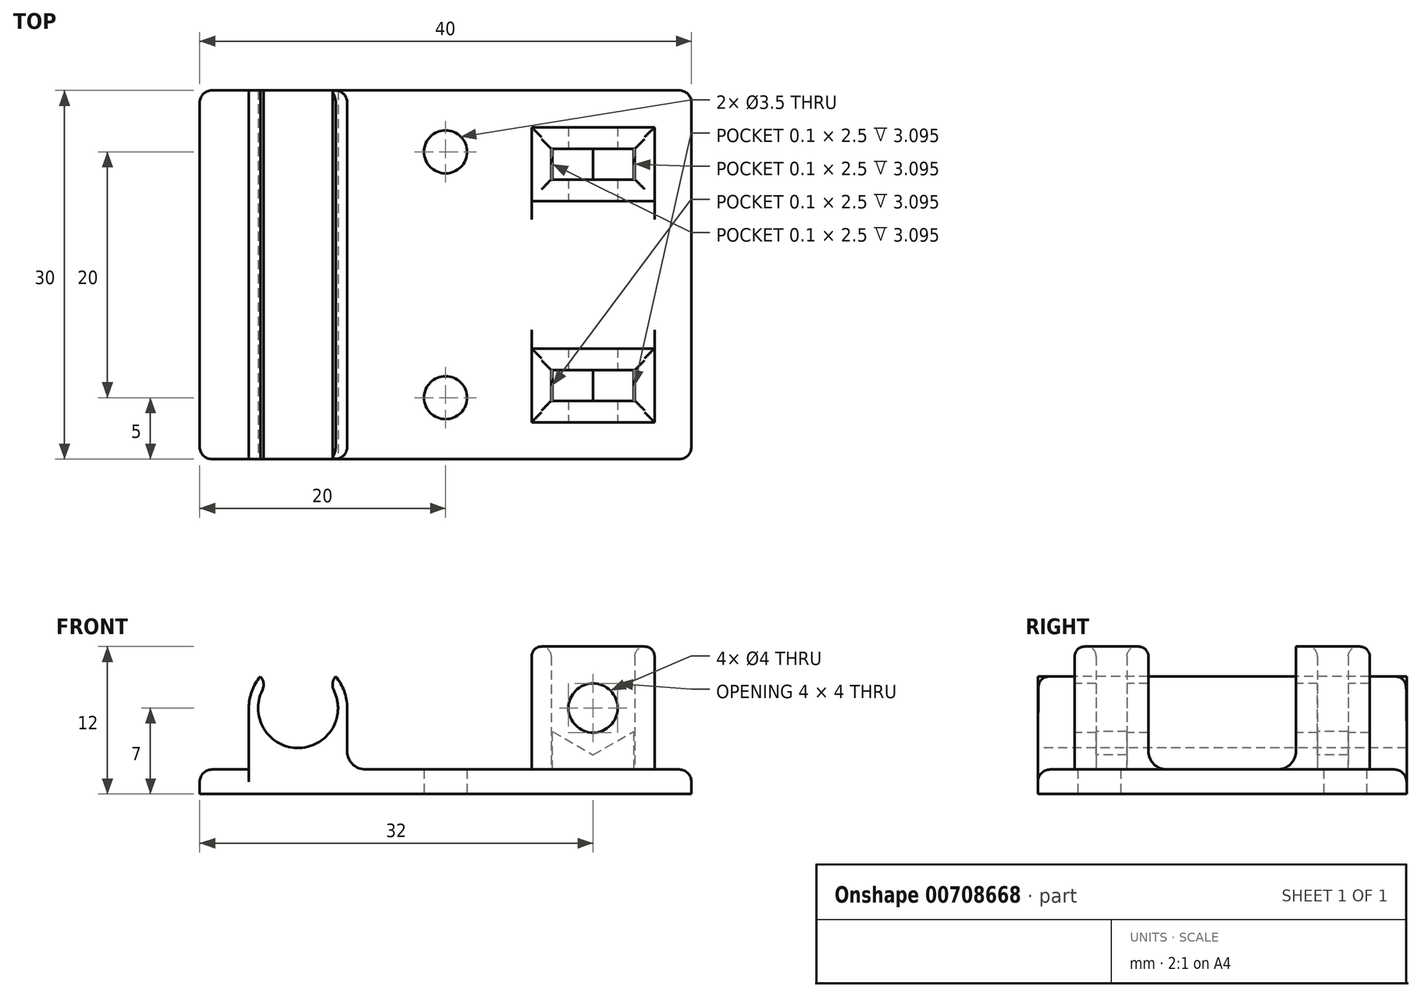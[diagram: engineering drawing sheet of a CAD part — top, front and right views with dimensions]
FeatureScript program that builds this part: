
annotation { "Feature Type Name" : "Feature", "Feature Type Description" : "" }
export const myFeature = defineFeature(function(context is Context, id is Id, definition is map)
    precondition{}
    {
        {
            var Q0;
            Q0=qCreatedBy(makeId("Top.planeOp"),FACE);
            var sketch = newSketch(context, id + "F0", { "sketchPlane" : qUnion([Q0])});
            skLineSegment(sketch, "E0.bottom", {"start": v(-20, 15) * mm, "end": v(20, 15) * mm});
            skLineSegment(sketch, "E0.top", {"start": v(-20, -15) * mm, "end": v(20, -15) * mm});
            skLineSegment(sketch, "E0.left", {"start": v(-20, 15) * mm, "end": v(-20, -15) * mm});
            skLineSegment(sketch, "E0.right", {"start": v(20, 15) * mm, "end": v(20, -15) * mm});
            skPoint(sketch, "E0.middle", {"position": v(0, 0) * mm});
            skLineSegment(sketch, "E1", {"start": v(12, 15) * mm, "end": v(12, 12) * mm, "construction": true});
            skLineSegment(sketch, "E2", {"start": v(7, -12) * mm, "end": v(17, -12) * mm});
            skLineSegment(sketch, "E3", {"start": v(17, -6) * mm, "end": v(7, -6) * mm});
            skLineSegment(sketch, "E4", {"start": v(7, 12) * mm, "end": v(17, 12) * mm});
            skLineSegment(sketch, "E5", {"start": v(17, -12) * mm, "end": v(17, -6) * mm});
            skLineSegment(sketch, "E6", {"start": v(17, 6) * mm, "end": v(7, 6) * mm});
            skLineSegment(sketch, "E7", {"start": v(7, 6) * mm, "end": v(7, 12) * mm});
            skLineSegment(sketch, "E8", {"start": v(17, 12) * mm, "end": v(17, 6) * mm});
            skLineSegment(sketch, "E9", {"start": v(7, -12) * mm, "end": v(7, -6) * mm});
            skLineSegment(sketch, "E10", {"start": v(12, 12) * mm, "end": v(12, 6) * mm, "construction": true});
            skLineSegment(sketch, "E11", {"start": v(12, 6) * mm, "end": v(12, -6) * mm, "construction": true});
            skLineSegment(sketch, "E12", {"start": v(12, -6) * mm, "end": v(12, -12) * mm, "construction": true});
            skLineSegment(sketch, "E13", {"start": v(12, -12) * mm, "end": v(12, -15) * mm, "construction": true});
            skLineSegment(sketch, "E14.bottom", {"start": v(8.6, -7.75) * mm, "end": v(15.4, -7.75) * mm});
            skLineSegment(sketch, "E14.top", {"start": v(8.6, -10.25) * mm, "end": v(15.4, -10.25) * mm});
            skLineSegment(sketch, "E14.left", {"start": v(8.6, -7.75) * mm, "end": v(8.6, -10.25) * mm});
            skLineSegment(sketch, "E14.right", {"start": v(15.4, -7.75) * mm, "end": v(15.4, -10.25) * mm});
            skPoint(sketch, "E14.middle", {"position": v(12, -9) * mm});
            skLineSegment(sketch, "E15.bottom", {"start": v(8.6, 7.75) * mm, "end": v(15.4, 7.75) * mm});
            skLineSegment(sketch, "E15.top", {"start": v(8.6, 10.25) * mm, "end": v(15.4, 10.25) * mm});
            skLineSegment(sketch, "E15.left", {"start": v(8.6, 7.75) * mm, "end": v(8.6, 10.25) * mm});
            skLineSegment(sketch, "E15.right", {"start": v(15.4, 7.75) * mm, "end": v(15.4, 10.25) * mm});
            skPoint(sketch, "E15.middle", {"position": v(12, 9) * mm});
            skLineSegment(sketch, "E16", {"start": v(7, -6) * mm, "end": v(7, 6) * mm});
            skLineSegment(sketch, "E17", {"start": v(17, 6) * mm, "end": v(17, -6) * mm});
            skLineSegment(sketch, "E18", {"start": v(-12, -15) * mm, "end": v(-12, 15) * mm, "construction": true});
            skCircle(sketch, "E19", {"center": v(0, 10) * mm, "radius": 1.75 * mm});
            skCircle(sketch, "E20", {"center": v(0, -10) * mm, "radius": 1.75 * mm});
            skSolve(sketch);
        }
        {
            var Q0;
            Q0=makeQuery(id+"F0.imprint","IMPRINT",FACE,{"disambiguationData":[TD([[makeQuery(id+"F0.imprint","IMPRINT",EDGE,{"derivedFrom":sQuery(id+"F0.wireOp",EDGE,"E0.bottom")}),-1.0]])]});
            var Q1;
            Q1=makeQuery(id+"F0.imprint","IMPRINT",FACE,{"disambiguationData":[TD([[makeQuery(id+"F0.imprint","IMPRINT",EDGE,{"derivedFrom":sQuery(id+"F0.wireOp",EDGE,"E15.bottom")}),1.0]])]});
            var Q2;
            Q2=makeQuery(id+"F0.imprint","IMPRINT",FACE,{"disambiguationData":[TD([[makeQuery(id+"F0.imprint","IMPRINT",EDGE,{"derivedFrom":sQuery(id+"F0.wireOp",EDGE,"E14.bottom")}),-1.0]])]});
            extrude(context, id + "F1", {"entities" : qUnion([Q0, Q1, Q2]), "depth" : 2 * mm, "offsetDistance" : 25 * mm});
        }
        {
            var Q0;
            Q0=makeQuery(id+"F0.imprint","IMPRINT",FACE,{"disambiguationData":[TD([[makeQuery(id+"F0.imprint","IMPRINT",EDGE,{"derivedFrom":sQuery(id+"F0.wireOp",EDGE,"E2")}),1.0]])]});
            var Q1;
            Q1=makeQuery(id+"F0.imprint","IMPRINT",FACE,{"disambiguationData":[TD([[makeQuery(id+"F0.imprint","IMPRINT",EDGE,{"derivedFrom":sQuery(id+"F0.wireOp",EDGE,"E4")}),-1.0]])]});
            var Q2;
            Q2=makeQuery(id+"F0.imprint","IMPRINT",FACE,{"disambiguationData":[TD([[makeQuery(id+"F0.imprint","IMPRINT",EDGE,{"derivedFrom":sQuery(id+"F0.wireOp",EDGE,"E3")}),-1.0]])]});
            extrude(context, id + "F2", {"entities" : qUnion([Q0, Q1, Q2]), "operationType" : NewBodyOperationType.ADD, "depth" : (2 + 10) * mm, "offsetDistance" : 25 * mm});
        }
        {
            var Q0;
            Q0=makeQuery(id+"F2.opExtrude","SWEPT_FACE",FACE,{"disambiguationData":[OSD([sQuery(id+"F0.wireOp",EDGE,"E2")])]});
            var sketch = newSketch(context, id + "F3", { "sketchPlane" : qUnion([Q0])});
            skLineSegment(sketch, "E21", {"start": v(7, 12) * mm, "end": v(17, 2) * mm, "construction": true});
            skCircle(sketch, "E22", {"center": v(12, 7) * mm, "radius": 2 * mm});
            skCircle(sketch, "E23.cCircle", {"center": v(12, 7) * mm, "radius": 3.3 * mm, "construction": true});
            skLineSegment(sketch, "E23.0", {"start": v(15.3, 8.9) * mm, "end": v(15.3, 5.1) * mm});
            skLineSegment(sketch, "E23.1", {"start": v(15.3, 5.1) * mm, "end": v(12, 3.19) * mm});
            skLineSegment(sketch, "E23.2", {"start": v(12, 3.19) * mm, "end": v(8.7, 5.1) * mm});
            skLineSegment(sketch, "E23.3", {"start": v(8.7, 5.1) * mm, "end": v(8.7, 8.9) * mm});
            skLineSegment(sketch, "E23.4", {"start": v(8.7, 8.9) * mm, "end": v(12, 10.81) * mm});
            skLineSegment(sketch, "E23.5", {"start": v(12, 10.81) * mm, "end": v(15.3, 8.9) * mm});
            skPoint(sketch, "E23.0.midPoint", {"position": v(15.3, 7) * mm});
            skLineSegment(sketch, "E24", {"start": v(8.7, 5.1) * mm, "end": v(8.7, 2) * mm});
            skLineSegment(sketch, "E25", {"start": v(8.7, 2) * mm, "end": v(15.3, 2) * mm});
            skLineSegment(sketch, "E26", {"start": v(15.3, 2) * mm, "end": v(15.3, 5.1) * mm});
            skSolve(sketch);
        }
        {
            var Q0;
            Q0=makeQuery(id+"F3.imprint","IMPRINT",FACE,{"disambiguationData":[TD([[makeQuery(id+"F3.imprint","IMPRINT",EDGE,{"derivedFrom":sQuery(id+"F3.wireOp",EDGE,"E22")}),1.0]])]});
            var Q1;
            Q1=makeQuery(id+"F2.opExtrude","SWEPT_FACE",FACE,{"disambiguationData":[OSD([sQuery(id+"F0.wireOp",EDGE,"E4")])]});
            extrude(context, id + "F4", {"entities" : qUnion([Q0]), "operationType" : NewBodyOperationType.REMOVE, "endBound" : BoundingType.UP_TO_SURFACE, "oppositeDirection" : true, "depth" : 25 * mm, "endBoundEntityFace" : qUnion([Q1]), "offsetDistance" : 25 * mm});
        }
        {
            var Q0;
            Q0=makeQuery(id+"F3.imprint","IMPRINT",FACE,{"disambiguationData":[TD([[makeQuery(id+"F3.imprint","IMPRINT",EDGE,{"derivedFrom":sQuery(id+"F3.wireOp",EDGE,"E23.1")}),1.0]])]});
            var Q1;
            Q1=makeQuery(id+"F2.opExtrude","SWEPT_FACE",FACE,{"disambiguationData":[OSD([sQuery(id+"F0.wireOp",EDGE,"E4")])]});
            extrude(context, id + "F5", {"entities" : qUnion([Q0]), "operationType" : NewBodyOperationType.ADD, "endBound" : BoundingType.UP_TO_SURFACE, "oppositeDirection" : true, "depth" : 25 * mm, "endBoundEntityFace" : qUnion([Q1]), "offsetDistance" : 25 * mm});
        }
        {
            var Q0;
            Q0=makeQuery(id+"F0.imprint","IMPRINT",FACE,{"disambiguationData":[TD([[makeQuery(id+"F0.imprint","IMPRINT",EDGE,{"derivedFrom":sQuery(id+"F0.wireOp",EDGE,"E3")}),-1.0]])]});
            var Q1;
            Q1=makeQuery(id+"F2.opExtrude","CAP_FACE",FACE,{"disambiguationData":[OSD([sQuery(id+"F0.wireOp",EDGE,"E2"),sQuery(id+"F0.wireOp",EDGE,"E4"),sQuery(id+"F0.wireOp",EDGE,"E5"),sQuery(id+"F0.wireOp",EDGE,"E7"),sQuery(id+"F0.wireOp",EDGE,"E8"),sQuery(id+"F0.wireOp",EDGE,"E9"),sQuery(id+"F0.wireOp",EDGE,"E14.bottom"),sQuery(id+"F0.wireOp",EDGE,"E14.top"),sQuery(id+"F0.wireOp",EDGE,"E14.left"),sQuery(id+"F0.wireOp",EDGE,"E14.right"),sQuery(id+"F0.wireOp",EDGE,"E15.bottom"),sQuery(id+"F0.wireOp",EDGE,"E15.top"),sQuery(id+"F0.wireOp",EDGE,"E15.left"),sQuery(id+"F0.wireOp",EDGE,"E15.right"),sQuery(id+"F0.wireOp",EDGE,"E16"),sQuery(id+"F0.wireOp",EDGE,"E17")])],"isStart":false});
            var Q2;
            Q2=makeQuery(id+"F1.opExtrude","CAP_FACE",FACE,{"disambiguationData":[OSD([sQuery(id+"F0.wireOp",EDGE,"E0.bottom"),sQuery(id+"F0.wireOp",EDGE,"E0.top"),sQuery(id+"F0.wireOp",EDGE,"E0.left"),sQuery(id+"F0.wireOp",EDGE,"E0.right"),sQuery(id+"F0.wireOp",EDGE,"E2"),sQuery(id+"F0.wireOp",EDGE,"E4"),sQuery(id+"F0.wireOp",EDGE,"E5"),sQuery(id+"F0.wireOp",EDGE,"E7"),sQuery(id+"F0.wireOp",EDGE,"E8"),sQuery(id+"F0.wireOp",EDGE,"E9"),sQuery(id+"F0.wireOp",EDGE,"E16"),sQuery(id+"F0.wireOp",EDGE,"E17")])],"isStart":false});
            extrude(context, id + "F6", {"entities" : qUnion([Q0]), "operationType" : NewBodyOperationType.REMOVE, "endBound" : BoundingType.UP_TO_SURFACE, "depth" : 25 * mm, "endBoundEntityFace" : qUnion([Q1]), "offsetDistance" : 25 * mm, "hasSecondDirection" : true, "secondDirectionBound" : SecondDirectionBoundingType.UP_TO_SURFACE, "secondDirectionOppositeDirection" : false, "secondDirectionDepth" : 1.62 * mm, "secondDirectionBoundEntityFace" : qUnion([Q2])});
        }
        {
            var Q0;
            Q0=makeQuery(id+"F1.opExtrude","CAP_EDGE",EDGE,{"disambiguationData":[OSD([sQuery(id+"F0.wireOp",EDGE,"E2")])],"isStart":false});
            var Q1;
            {var subQ1=sQuery(id+"F0.wireOp",EDGE,"E17");var subQ2=sQuery(id+"F0.wireOp",EDGE,"E8");var subQ3=sQuery(id+"F0.wireOp",EDGE,"E5");var subQ4=sQuery(id+"F0.wireOp",EDGE,"E2");Q1=makeQuery(id+"F6.boolean.opBoolean","SPLIT",EDGE,{"disambiguationData":[TD([makeQuery(id+"F2.opExtrude","SWEPT_FACE",FACE,{"disambiguationData":[OSD([subQ4])]})])],"derivedFrom":makeQuery(id+"F1.opExtrude","CAP_EDGE",EDGE,{"disambiguationData":[OSD([subQ3,subQ2,subQ1])],"isStart":false})});}
            var Q2;
            Q2=makeQuery(id+"F6.boolean.opBoolean","COPY",EDGE,{"derivedFrom":makeQuery(id+"F6.opExtrude","CAP_EDGE",EDGE,{"disambiguationData":[OSD([sQuery(id+"F0.wireOp",EDGE,"E3")])],"isStart":true})});
            var Q3;
            {var subQ1=sQuery(id+"F0.wireOp",EDGE,"E16");var subQ2=sQuery(id+"F0.wireOp",EDGE,"E9");var subQ3=sQuery(id+"F0.wireOp",EDGE,"E7");var subQ4=sQuery(id+"F0.wireOp",EDGE,"E2");Q3=makeQuery(id+"F6.boolean.opBoolean","SPLIT",EDGE,{"disambiguationData":[TD([makeQuery(id+"F2.opExtrude","SWEPT_FACE",FACE,{"disambiguationData":[OSD([subQ4])]})])],"derivedFrom":makeQuery(id+"F1.opExtrude","CAP_EDGE",EDGE,{"disambiguationData":[OSD([subQ3,subQ2,subQ1])],"isStart":false})});}
            var Q4;
            Q4=makeQuery(id+"F6.boolean.opBoolean","COPY",EDGE,{"derivedFrom":makeQuery(id+"F6.opExtrude","CAP_EDGE",EDGE,{"disambiguationData":[OSD([sQuery(id+"F0.wireOp",EDGE,"E6")])],"isStart":true})});
            var Q5;
            {var subQ1=sQuery(id+"F0.wireOp",EDGE,"E16");var subQ3=sQuery(id+"F0.wireOp",EDGE,"E9");var subQ4=sQuery(id+"F0.wireOp",EDGE,"E7");var subQ5=sQuery(id+"F0.wireOp",EDGE,"E4");Q5=makeQuery(id+"F6.boolean.opBoolean","SPLIT",EDGE,{"disambiguationData":[TD([makeQuery(id+"F2.opExtrude","SWEPT_FACE",FACE,{"disambiguationData":[OSD([subQ5])]})])],"derivedFrom":makeQuery(id+"F1.opExtrude","CAP_EDGE",EDGE,{"disambiguationData":[OSD([subQ4,subQ3,subQ1])],"isStart":false})});}
            var Q6;
            {var subQ0=sQuery(id+"F0.wireOp",EDGE,"E17");var subQ3=sQuery(id+"F0.wireOp",EDGE,"E8");var subQ4=sQuery(id+"F0.wireOp",EDGE,"E5");var subQ5=sQuery(id+"F0.wireOp",EDGE,"E4");Q6=makeQuery(id+"F6.boolean.opBoolean","SPLIT",EDGE,{"disambiguationData":[TD([makeQuery(id+"F2.opExtrude","SWEPT_FACE",FACE,{"disambiguationData":[OSD([subQ5])]})])],"derivedFrom":makeQuery(id+"F1.opExtrude","CAP_EDGE",EDGE,{"disambiguationData":[OSD([subQ4,subQ3,subQ0])],"isStart":false})});}
            var Q7;
            Q7=makeQuery(id+"F1.opExtrude","CAP_EDGE",EDGE,{"disambiguationData":[OSD([sQuery(id+"F0.wireOp",EDGE,"E4")])],"isStart":false});
            fillet(context, id + "F7", {"entities" : qUnion([Q0, Q1, Q2, Q3, Q4, Q5, Q6, Q7]), "radius" : 1.5 * mm, "tangentPropagation" : true, "allowEdgeOverflow" : false});
        }
        {
            var Q0;
            Q0=makeQuery(id+"F2.opExtrude","CAP_EDGE",EDGE,{"disambiguationData":[OSD([sQuery(id+"F0.wireOp",EDGE,"E14.top")])],"isStart":false});
            var Q1;
            Q1=makeQuery(id+"F2.opExtrude","CAP_EDGE",EDGE,{"disambiguationData":[OSD([sQuery(id+"F0.wireOp",EDGE,"E14.left")])],"isStart":false});
            var Q2;
            Q2=makeQuery(id+"F2.opExtrude","CAP_EDGE",EDGE,{"disambiguationData":[OSD([sQuery(id+"F0.wireOp",EDGE,"E14.bottom")])],"isStart":false});
            var Q3;
            Q3=makeQuery(id+"F2.opExtrude","CAP_EDGE",EDGE,{"disambiguationData":[OSD([sQuery(id+"F0.wireOp",EDGE,"E14.right")])],"isStart":false});
            var Q4;
            {var subQ0=sQuery(id+"F0.wireOp",EDGE,"E2");var subQ1=sQuery(id+"F0.wireOp",EDGE,"E17");var subQ2=sQuery(id+"F0.wireOp",EDGE,"E8");var subQ3=sQuery(id+"F0.wireOp",EDGE,"E5");Q4=makeQuery(id+"F6.boolean.opBoolean","SPLIT",EDGE,{"disambiguationData":[TD([makeQuery(id+"F2.opExtrude","SWEPT_FACE",FACE,{"disambiguationData":[OSD([subQ0])]})])],"derivedFrom":makeQuery(id+"F2.opExtrude","CAP_EDGE",EDGE,{"disambiguationData":[OSD([subQ3,subQ2,subQ1])],"isStart":false})});}
            var Q5;
            Q5=makeQuery(id+"F2.opExtrude","CAP_EDGE",EDGE,{"disambiguationData":[OSD([sQuery(id+"F0.wireOp",EDGE,"E2")])],"isStart":false});
            var Q6;
            Q6=makeQuery(id+"F6.boolean.opBoolean","COPY",EDGE,{"derivedFrom":makeQuery(id+"F6.opExtrude","CAP_EDGE",EDGE,{"disambiguationData":[OSD([sQuery(id+"F0.wireOp",EDGE,"E3")])],"isStart":false})});
            var Q7;
            {var subQ0=sQuery(id+"F0.wireOp",EDGE,"E2");var subQ1=sQuery(id+"F0.wireOp",EDGE,"E16");var subQ2=sQuery(id+"F0.wireOp",EDGE,"E9");var subQ3=sQuery(id+"F0.wireOp",EDGE,"E7");Q7=makeQuery(id+"F6.boolean.opBoolean","SPLIT",EDGE,{"disambiguationData":[TD([makeQuery(id+"F2.opExtrude","SWEPT_FACE",FACE,{"disambiguationData":[OSD([subQ0])]})])],"derivedFrom":makeQuery(id+"F2.opExtrude","CAP_EDGE",EDGE,{"disambiguationData":[OSD([subQ3,subQ2,subQ1])],"isStart":false})});}
            var Q8;
            Q8=makeQuery(id+"F6.boolean.opBoolean","COPY",EDGE,{"derivedFrom":makeQuery(id+"F6.opExtrude","CAP_EDGE",EDGE,{"disambiguationData":[OSD([sQuery(id+"F0.wireOp",EDGE,"E6")])],"isStart":false})});
            var Q9;
            {var subQ0=sQuery(id+"F0.wireOp",EDGE,"E16");var subQ1=sQuery(id+"F0.wireOp",EDGE,"E9");var subQ2=sQuery(id+"F0.wireOp",EDGE,"E7");var subQ3=sQuery(id+"F0.wireOp",EDGE,"E4");Q9=makeQuery(id+"F6.boolean.opBoolean","SPLIT",EDGE,{"disambiguationData":[TD([makeQuery(id+"F2.opExtrude","SWEPT_FACE",FACE,{"disambiguationData":[OSD([subQ3])]})])],"derivedFrom":makeQuery(id+"F2.opExtrude","CAP_EDGE",EDGE,{"disambiguationData":[OSD([subQ2,subQ1,subQ0])],"isStart":false})});}
            var Q10;
            Q10=makeQuery(id+"F2.opExtrude","CAP_EDGE",EDGE,{"disambiguationData":[OSD([sQuery(id+"F0.wireOp",EDGE,"E4")])],"isStart":false});
            var Q11;
            {var subQ0=sQuery(id+"F0.wireOp",EDGE,"E17");var subQ1=sQuery(id+"F0.wireOp",EDGE,"E8");var subQ2=sQuery(id+"F0.wireOp",EDGE,"E5");var subQ3=sQuery(id+"F0.wireOp",EDGE,"E4");Q11=makeQuery(id+"F6.boolean.opBoolean","SPLIT",EDGE,{"disambiguationData":[TD([makeQuery(id+"F2.opExtrude","SWEPT_FACE",FACE,{"disambiguationData":[OSD([subQ3])]})])],"derivedFrom":makeQuery(id+"F2.opExtrude","CAP_EDGE",EDGE,{"disambiguationData":[OSD([subQ2,subQ1,subQ0])],"isStart":false})});}
            var Q12;
            Q12=makeQuery(id+"F2.opExtrude","CAP_EDGE",EDGE,{"disambiguationData":[OSD([sQuery(id+"F0.wireOp",EDGE,"E15.right")])],"isStart":false});
            var Q13;
            Q13=makeQuery(id+"F2.opExtrude","CAP_EDGE",EDGE,{"disambiguationData":[OSD([sQuery(id+"F0.wireOp",EDGE,"E15.top")])],"isStart":false});
            var Q14;
            Q14=makeQuery(id+"F2.opExtrude","CAP_EDGE",EDGE,{"disambiguationData":[OSD([sQuery(id+"F0.wireOp",EDGE,"E15.bottom")])],"isStart":false});
            var Q15;
            Q15=makeQuery(id+"F2.opExtrude","CAP_EDGE",EDGE,{"disambiguationData":[OSD([sQuery(id+"F0.wireOp",EDGE,"E15.left")])],"isStart":false});
            fillet(context, id + "F8", {"entities" : qUnion([Q0, Q1, Q2, Q3, Q4, Q5, Q6, Q7, Q8, Q9, Q10, Q11, Q12, Q13, Q14, Q15]), "radius" : 0.8 * mm, "tangentPropagation" : true, "allowEdgeOverflow" : false});
        }
        {
            var Q0;
            Q0=sQuery(id+"F0.wireOp",VERTEX,"E18.start");
            var Q1;
            Q1=sQuery(id+"F0.wireOp",EDGE,"E18");
            cPlane(context, id + "F9", {"entities" : qUnion([Q0, Q1]), "cplaneType" : CPlaneType.LINE_POINT, "offset" : 25 * mm, "width" : 150 * mm, "height" : 150 * mm});
        }
        {
            var Q0;
            Q0=qCreatedBy(id+"F9.planeOp",FACE);
            var sketch = newSketch(context, id + "F10", { "sketchPlane" : qUnion([Q0])});
            skPoint(sketch, "E27.0", {"position": v(12, 0) * mm});
            skLineSegment(sketch, "E28.0", {"start": v(20, 2) * mm, "end": v(-20, 2) * mm});
            skCircle(sketch, "E29", {"center": v(12, 7) * mm, "radius": 3.25 * mm});
            skArc(sketch, "E30", {"start": v(16, 7) * mm, "mid": v(12, 11) * mm, "end": v(8, 7) * mm});
            skLineSegment(sketch, "E31", {"start": v(16, 7) * mm, "end": v(16, 2) * mm});
            skLineSegment(sketch, "E32", {"start": v(8, 7) * mm, "end": v(8, 2) * mm});
            skLineSegment(sketch, "E33", {"start": v(12, 7) * mm, "end": v(15.06, 9.57) * mm});
            skLineSegment(sketch, "E34", {"start": v(12, 7) * mm, "end": v(8.94, 9.57) * mm});
            skSolve(sketch);
        }
        {
            var Q0;
            {var subQ0=sQuery(id+"F10.wireOp",EDGE,"E31");Q0=makeQuery(id+"F10.imprint","IMPRINT",FACE,{"disambiguationData":[TD([[makeQuery(id+"F10.imprint","IMPRINT",EDGE,{"derivedFrom":subQ0}),-1.0]])]});}
            var Q1;
            {var subQ0=sQuery(id+"F10.wireOp",EDGE,"E32");Q1=makeQuery(id+"F10.imprint","IMPRINT",FACE,{"disambiguationData":[TD([[makeQuery(id+"F10.imprint","IMPRINT",EDGE,{"derivedFrom":subQ0}),1.0]])]});}
            var Q2;
            Q2=makeQuery(id+"F1.opExtrude","SWEPT_FACE",FACE,{"disambiguationData":[OSD([sQuery(id+"F0.wireOp",EDGE,"E0.bottom")])]});
            extrude(context, id + "F11", {"entities" : qUnion([Q0, Q1]), "operationType" : NewBodyOperationType.ADD, "endBound" : BoundingType.UP_TO_SURFACE, "depth" : 29.6 * mm, "endBoundEntityFace" : qUnion([Q2]), "offsetDistance" : 25 * mm});
        }
        {
            var Q0;
            Q0=makeQuery(id+"F11.opExtrude","SWEPT_EDGE",EDGE,{"disambiguationData":[OSD([sQuery(id+"F10.wireOp",EDGE,"E29"),sQuery(id+"F10.wireOp",EDGE,"E33")])]});
            var Q1;
            Q1=makeQuery(id+"F11.opExtrude","SWEPT_EDGE",EDGE,{"disambiguationData":[OSD([sQuery(id+"F10.wireOp",EDGE,"E29"),sQuery(id+"F10.wireOp",EDGE,"E34")])]});
            fillet(context, id + "F12", {"entities" : qUnion([Q0, Q1]), "radius" : 1 * mm, "tangentPropagation" : true, "allowEdgeOverflow" : false});
        }
        {
            var Q0;
            Q0=makeQuery(id+"F11.opExtrude","SWEPT_EDGE",EDGE,{"disambiguationData":[OSD([sQuery(id+"F10.wireOp",EDGE,"E28.0"),sQuery(id+"F10.wireOp",EDGE,"E31")])]});
            var Q1;
            Q1=makeQuery(id+"F11.opExtrude","SWEPT_EDGE",EDGE,{"disambiguationData":[OSD([sQuery(id+"F10.wireOp",EDGE,"E28.0"),sQuery(id+"F10.wireOp",EDGE,"E32")])]});
            fillet(context, id + "F13", {"entities" : qUnion([Q0, Q1]), "radius" : 1.5 * mm, "tangentPropagation" : true, "allowEdgeOverflow" : false});
        }
        {
            var Q0;
            Q0=makeQuery(id+"F1.opExtrude","SWEPT_EDGE",EDGE,{"disambiguationData":[OSD([sQuery(id+"F0.wireOp",EDGE,"E0.top"),sQuery(id+"F0.wireOp",EDGE,"E0.left")])]});
            var Q1;
            Q1=makeQuery(id+"F1.opExtrude","CAP_EDGE",EDGE,{"disambiguationData":[OSD([sQuery(id+"F0.wireOp",EDGE,"E0.left")])],"isStart":false});
            var Q2;
            {var subQ1=sQuery(id+"F0.wireOp",EDGE,"E0.bottom");var subQ2=sQuery(id+"F0.wireOp",EDGE,"E0.left");Q2=makeQuery(id+"F11.boolean.opBoolean","SPLIT",EDGE,{"disambiguationData":[TD([makeQuery(id+"F1.opExtrude","SWEPT_FACE",FACE,{"disambiguationData":[OSD([subQ2])]})])],"derivedFrom":makeQuery(id+"F1.opExtrude","CAP_EDGE",EDGE,{"disambiguationData":[OSD([subQ1])],"isStart":false})});}
            var Q3;
            {var subQ0=sQuery(id+"F0.wireOp",EDGE,"E0.left");var subQ2=sQuery(id+"F0.wireOp",EDGE,"E0.top");Q3=makeQuery(id+"F11.boolean.opBoolean","SPLIT",EDGE,{"disambiguationData":[TD([makeQuery(id+"F1.opExtrude","SWEPT_FACE",FACE,{"disambiguationData":[OSD([subQ0])]})])],"derivedFrom":makeQuery(id+"F1.opExtrude","CAP_EDGE",EDGE,{"disambiguationData":[OSD([subQ2])],"isStart":false})});}
            var Q4;
            Q4=makeQuery(id+"F1.opExtrude","SWEPT_EDGE",EDGE,{"disambiguationData":[OSD([sQuery(id+"F0.wireOp",EDGE,"E0.bottom"),sQuery(id+"F0.wireOp",EDGE,"E0.left")])]});
            var Q5;
            {var subQ1=sQuery(id+"F0.wireOp",EDGE,"E0.bottom");var subQ2=sQuery(id+"F0.wireOp",EDGE,"E0.right");Q5=makeQuery(id+"F11.boolean.opBoolean","SPLIT",EDGE,{"disambiguationData":[TD([makeQuery(id+"F1.opExtrude","SWEPT_FACE",FACE,{"disambiguationData":[OSD([subQ2])]})])],"derivedFrom":makeQuery(id+"F1.opExtrude","CAP_EDGE",EDGE,{"disambiguationData":[OSD([subQ1])],"isStart":false})});}
            var Q6;
            Q6=makeQuery(id+"F1.opExtrude","CAP_EDGE",EDGE,{"disambiguationData":[OSD([sQuery(id+"F0.wireOp",EDGE,"E0.right")])],"isStart":false});
            var Q7;
            Q7=makeQuery(id+"F1.opExtrude","SWEPT_EDGE",EDGE,{"disambiguationData":[OSD([sQuery(id+"F0.wireOp",EDGE,"E0.bottom"),sQuery(id+"F0.wireOp",EDGE,"E0.right")])]});
            var Q8;
            {var subQ0=sQuery(id+"F0.wireOp",EDGE,"E0.right");var subQ2=sQuery(id+"F0.wireOp",EDGE,"E0.top");Q8=makeQuery(id+"F11.boolean.opBoolean","SPLIT",EDGE,{"disambiguationData":[TD([makeQuery(id+"F1.opExtrude","SWEPT_FACE",FACE,{"disambiguationData":[OSD([subQ0])]})])],"derivedFrom":makeQuery(id+"F1.opExtrude","CAP_EDGE",EDGE,{"disambiguationData":[OSD([subQ2])],"isStart":false})});}
            var Q9;
            Q9=makeQuery(id+"F1.opExtrude","SWEPT_EDGE",EDGE,{"disambiguationData":[OSD([sQuery(id+"F0.wireOp",EDGE,"E0.top"),sQuery(id+"F0.wireOp",EDGE,"E0.right")])]});
            fillet(context, id + "F14", {"entities" : qUnion([Q0, Q1, Q2, Q3, Q4, Q5, Q6, Q7, Q8, Q9]), "radius" : 1 * mm, "tangentPropagation" : true, "allowEdgeOverflow" : false});
        }
    });
